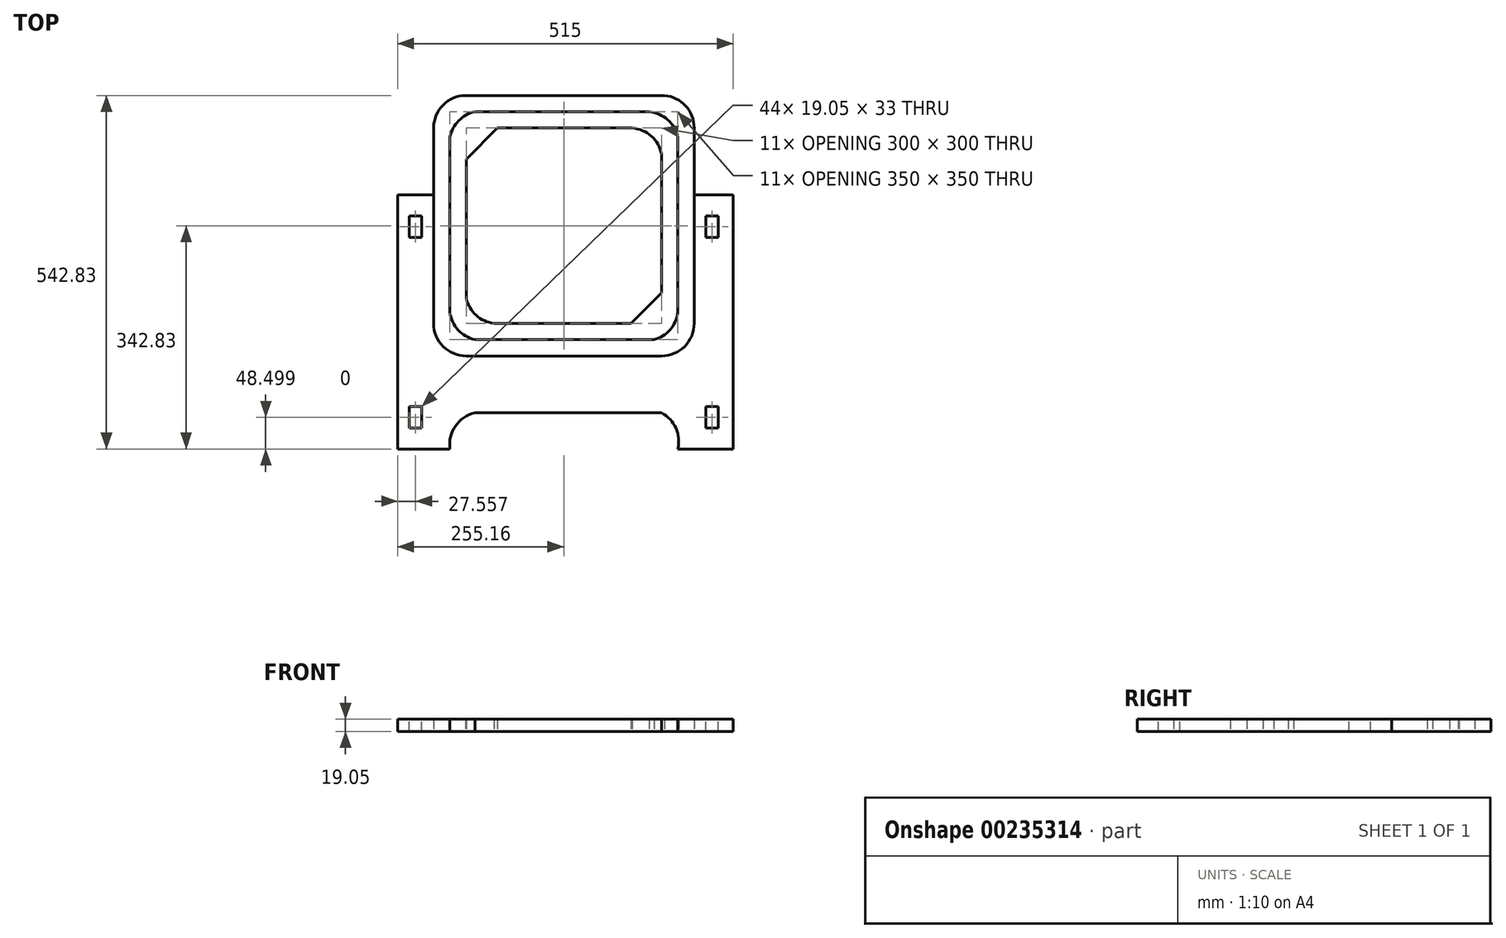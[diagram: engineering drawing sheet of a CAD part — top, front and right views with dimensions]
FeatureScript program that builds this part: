
annotation { "Feature Type Name" : "Feature", "Feature Type Description" : "" }
export const myFeature = defineFeature(function(context is Context, id is Id, definition is map)
    precondition{}
    {
        {
            var Q0;
            Q0=qCreatedBy(makeId("Top.planeOp"),FACE);
            var sketch = newSketch(context, id + "F0", { "sketchPlane" : qUnion([Q0])});
            skLineSegment(sketch, "E0.bottom", {"start": v(-150.99, 200) * mm, "end": v(154.38, 200) * mm});
            skLineSegment(sketch, "E0.top", {"start": v(-150, -200) * mm, "end": v(150, -200) * mm});
            skLineSegment(sketch, "E0.left", {"start": v(-200, 150.95) * mm, "end": v(-200, -150) * mm});
            skLineSegment(sketch, "E0.right", {"start": v(200, 150.38) * mm, "end": v(200, -150) * mm});
            skPoint(sketch, "E0.middle", {"position": v(0, 0) * mm});
            skLineSegment(sketch, "E1.bottom", {"start": v(-136.63, 175) * mm, "end": v(130.7, 175) * mm});
            skLineSegment(sketch, "E1.top", {"start": v(-136.63, -175) * mm, "end": v(138.66, -175) * mm});
            skLineSegment(sketch, "E1.left", {"start": v(-175, 136.37) * mm, "end": v(-175, -133.3) * mm});
            skLineSegment(sketch, "E1.right", {"start": v(175, 136.37) * mm, "end": v(175, -133.3) * mm});
            skLineSegment(sketch, "E2.bottom", {"start": v(-102.26, 150) * mm, "end": v(104.86, 150) * mm});
            skLineSegment(sketch, "E2.top", {"start": v(-107.07, -150) * mm, "end": v(102.92, -150) * mm});
            skLineSegment(sketch, "E2.left", {"start": v(-150, 102.12) * mm, "end": v(-150, -111.41) * mm});
            skLineSegment(sketch, "E2.right", {"start": v(150, 110.12) * mm, "end": v(150, -102.78) * mm});
            skLineSegment(sketch, "E3.bottom", {"start": v(-255.16, -342.83) * mm, "end": v(-175, -342.83) * mm});
            skLineSegment(sketch, "E3.top", {"start": v(-255.16, 47.17) * mm, "end": v(-200, 47.17) * mm});
            skLineSegment(sketch, "E3.left", {"start": v(-255.16, -342.83) * mm, "end": v(-255.16, 47.17) * mm});
            skLineSegment(sketch, "E3.right", {"start": v(259.84, -342.83) * mm, "end": v(259.84, 47.17) * mm});
            skArc(sketch, "E4", {"start": v(-149.03, 200) * mm, "mid": v(-184.68, 186.04) * mm, "end": v(-200, 150.95) * mm});
            skArc(sketch, "E5", {"start": v(200, 150) * mm, "mid": v(183.84, 187) * mm, "end": v(145.62, 200) * mm});
            skArc(sketch, "E6", {"start": v(-200, -150) * mm, "mid": v(-185.36, -185.36) * mm, "end": v(-150, -200) * mm});
            skArc(sketch, "E7", {"start": v(150, -200) * mm, "mid": v(185.36, -185.36) * mm, "end": v(200, -150) * mm});
            skPoint(sketch, "E8.orphan", {"position": v(200, -200) * mm});
            skPoint(sketch, "E9.orphan", {"position": v(-200, -200) * mm});
            skPoint(sketch, "E10.orphan", {"position": v(200, 200) * mm});
            skPoint(sketch, "E11.orphan", {"position": v(-200, 200) * mm});
            skArc(sketch, "E12", {"start": v(-136.63, 175) * mm, "mid": v(-161.54, 161.36) * mm, "end": v(-175, 136.37) * mm});
            skArc(sketch, "E13", {"start": v(175, 136.37) * mm, "mid": v(159.13, 162.88) * mm, "end": v(130.7, 175) * mm});
            skArc(sketch, "E14", {"start": v(-175, -133.3) * mm, "mid": v(-162.3, -160.1) * mm, "end": v(-136.63, -175) * mm});
            skArc(sketch, "E15", {"start": v(138.66, -175) * mm, "mid": v(163.12, -159.63) * mm, "end": v(175, -133.3) * mm});
            skArc(sketch, "E16", {"start": v(-136.63, -287.4) * mm, "mid": v(-166.56, -307.67) * mm, "end": v(-175, -342.83) * mm});
            skArc(sketch, "E17", {"start": v(175, -342.83) * mm, "mid": v(171.9, -310.87) * mm, "end": v(150, -287.4) * mm});
            skLineSegment(sketch, "E18", {"start": v(-136.63, -287.4) * mm, "end": v(150, -287.4) * mm});
            skLineSegment(sketch, "E19.trimOffspring", {"start": v(175, -342.83) * mm, "end": v(259.84, -342.83) * mm});
            skArc(sketch, "E20", {"start": v(150, 110.12) * mm, "mid": v(134.1, 137.62) * mm, "end": v(104.86, 150) * mm});
            skArc(sketch, "E21", {"start": v(-150, -111.41) * mm, "mid": v(-134.67, -137.53) * mm, "end": v(-107.07, -150) * mm});
            skCircle(sketch, "E22", {"center": v(-54.99, 56.8) * mm, "radius": 42.5 * mm});
            skCircle(sketch, "E23", {"center": v(-54.99, -35.11) * mm, "radius": 27.5 * mm});
            skArc(sketch, "E24", {"start": v(35.46, 73.38) * mm, "mid": v(20.46, 88.38) * mm, "end": v(5.46, 73.38) * mm});
            skArc(sketch, "E25", {"start": v(45.8, -43.7) * mm, "mid": v(60.8, -58.7) * mm, "end": v(75.8, -43.7) * mm});
            skArc(sketch, "E26", {"start": v(43.9, 89.17) * mm, "mid": v(37.47, 72.1) * mm, "end": v(45.8, 55.87) * mm});
            skArc(sketch, "E27", {"start": v(5.46, -26.92) * mm, "mid": v(-2.03, -42.98) * mm, "end": v(4.43, -59.48) * mm});
            skLineSegment(sketch, "E28", {"start": v(75.8, -43.7) * mm, "end": v(75.8, 57.42) * mm});
            skLineSegment(sketch, "E29", {"start": v(45.8, -43.7) * mm, "end": v(45.8, 55.87) * mm});
            skLineSegment(sketch, "E30", {"start": v(35.46, 73.38) * mm, "end": v(35.46, -26.92) * mm});
            skLineSegment(sketch, "E31", {"start": v(5.46, 73.38) * mm, "end": v(5.46, -26.92) * mm});
            skArc(sketch, "E32", {"start": v(72.87, -93.57) * mm, "mid": v(96.16, -81.07) * mm, "end": v(72.87, -68.57) * mm});
            skArc(sketch, "E33", {"start": v(-16.83, -68.57) * mm, "mid": v(-29.33, -81.07) * mm, "end": v(-16.83, -93.57) * mm});
            skLineSegment(sketch, "E34", {"start": v(-16.83, -68.57) * mm, "end": v(72.87, -68.57) * mm});
            skLineSegment(sketch, "E35", {"start": v(-16.83, -93.57) * mm, "end": v(72.87, -93.57) * mm});
            skArc(sketch, "E36.trimOffspring", {"start": v(75.8, 57.42) * mm, "mid": v(82.43, 73.26) * mm, "end": v(75.96, 89.17) * mm});
            skPoint(sketch, "E37.start.orphan", {"position": v(59.93, 89.17) * mm});
            skLineSegment(sketch, "E38", {"start": v(43.9, 89.17) * mm, "end": v(75.96, 89.17) * mm});
            skLineSegment(sketch, "E39", {"start": v(59.93, 73.38) * mm, "end": v(59.93, 89.17) * mm, "construction": true});
            skArc(sketch, "E40.trimOffspring", {"start": v(36.48, -59.48) * mm, "mid": v(42.94, -42.98) * mm, "end": v(35.46, -26.92) * mm});
            skLineSegment(sketch, "E41", {"start": v(4.43, -59.48) * mm, "end": v(36.48, -59.48) * mm});
            skLineSegment(sketch, "E42", {"start": v(125.43, -126.78) * mm, "end": v(150, -150) * mm, "construction": true});
            skLineSegment(sketch, "E43", {"start": v(-126.06, 126.13) * mm, "end": v(-150, 102.12) * mm});
            skLineSegment(sketch, "E44", {"start": v(-126.06, 126.13) * mm, "end": v(-102.26, 150) * mm});
            skLineSegment(sketch, "E45", {"start": v(126.63, -126.22) * mm, "end": v(102.7, -150.23) * mm});
            skLineSegment(sketch, "E46", {"start": v(126.63, -126.22) * mm, "end": v(150.43, -102.35) * mm});
            skLineSegment(sketch, "E47.trimOffspring", {"start": v(200, 47.17) * mm, "end": v(259.84, 47.17) * mm});
            skPoint(sketch, "E48.orphan", {"position": v(-175, 175) * mm});
            skPoint(sketch, "E49.orphan", {"position": v(175, 175) * mm});
            skPoint(sketch, "E50.orphan", {"position": v(175, -175) * mm});
            skPoint(sketch, "E51.orphan", {"position": v(-175, -175) * mm});
            skPoint(sketch, "E52.orphan", {"position": v(150, 150) * mm});
            skLineSegment(sketch, "E53.bottom", {"start": v(-110, 110) * mm, "end": v(110, 110) * mm});
            skLineSegment(sketch, "E53.top", {"start": v(-110, -110) * mm, "end": v(110, -110) * mm});
            skLineSegment(sketch, "E53.left", {"start": v(-110, 110) * mm, "end": v(-110, -110) * mm});
            skLineSegment(sketch, "E53.right", {"start": v(110, 110) * mm, "end": v(110, -110) * mm});
            skLineSegment(sketch, "E54", {"start": v(-110, -110) * mm, "end": v(-92.32, -92.32) * mm});
            skLineSegment(sketch, "E55", {"start": v(-74.64, -110) * mm, "end": v(-110, -74.64) * mm});
            skLineSegment(sketch, "E56", {"start": v(110, 73.38) * mm, "end": v(75.96, 110) * mm});
            skLineSegment(sketch, "E57.trimOffspring", {"start": v(92.36, 92.36) * mm, "end": v(110, 110) * mm});
            skSolve(sketch);
        }
        {
            var Q0;
            Q0=makeQuery(id+"F0.imprint","IMPRINT",FACE,{"disambiguationData":[TD([[makeQuery(id+"F0.imprint","IMPRINT",EDGE,{"derivedFrom":sQuery(id+"F0.wireOp",EDGE,"E0.top")}),-1.0]])]});
            extrude(context, id + "F1", {"entities" : qUnion([Q0]), "depth" : 19.05 * mm});
        }
        {
            var Q0;
            Q0=makeQuery(id+"F0.imprint","IMPRINT",FACE,{"disambiguationData":[TD([[makeQuery(id+"F0.imprint","IMPRINT",EDGE,{"derivedFrom":sQuery(id+"F0.wireOp",EDGE,"E0.top")}),1.0]])]});
            extrude(context, id + "F2", {"entities" : qUnion([Q0]), "depth" : 19.05 * mm});
        }
        {
            var Q0;
            Q0=makeQuery(id+"F0.imprint","IMPRINT",FACE,{"disambiguationData":[TD([[makeQuery(id+"F0.imprint","IMPRINT",EDGE,{"derivedFrom":sQuery(id+"F0.wireOp",EDGE,"E1.bottom")}),-1.0]])]});
            extrude(context, id + "F3", {"entities" : qUnion([Q0]), "depth" : 19.05 * mm});
        }
        {
            var Q0;
            Q0=makeQuery(id+"F1.opExtrude","CAP_FACE",FACE,{"disambiguationData":[OSD([sQuery(id+"F0.wireOp",EDGE,"E0.top"),sQuery(id+"F0.wireOp",EDGE,"E0.left"),sQuery(id+"F0.wireOp",EDGE,"E0.right"),sQuery(id+"F0.wireOp",EDGE,"E3.bottom"),sQuery(id+"F0.wireOp",EDGE,"E3.top"),sQuery(id+"F0.wireOp",EDGE,"E3.left"),sQuery(id+"F0.wireOp",EDGE,"E3.right"),sQuery(id+"F0.wireOp",EDGE,"E6"),sQuery(id+"F0.wireOp",EDGE,"E7"),sQuery(id+"F0.wireOp",EDGE,"E16"),sQuery(id+"F0.wireOp",EDGE,"E17"),sQuery(id+"F0.wireOp",EDGE,"E18"),sQuery(id+"F0.wireOp",EDGE,"E19.trimOffspring"),sQuery(id+"F0.wireOp",EDGE,"E47.trimOffspring")])],"isStart":false});
            var sketch = newSketch(context, id + "F4", { "sketchPlane" : qUnion([Q0])});
            skLineSegment(sketch, "E58.bottom", {"start": v(-237.13, 15.17) * mm, "end": v(-218.08, 15.17) * mm});
            skLineSegment(sketch, "E58.top", {"start": v(-237.13, -17.83) * mm, "end": v(-218.08, -17.83) * mm});
            skLineSegment(sketch, "E58.left", {"start": v(-237.13, 15.17) * mm, "end": v(-237.13, -17.83) * mm});
            skLineSegment(sketch, "E58.right", {"start": v(-218.08, 15.17) * mm, "end": v(-218.08, -17.83) * mm});
            skLineSegment(sketch, "E59", {"start": v(-227.58, 47.17) * mm, "end": v(-227.58, -342.83) * mm, "construction": true});
            skPoint(sketch, "E59.endSnap0", {"position": v(-215.08, -342.83) * mm});
            skLineSegment(sketch, "E60.bottom", {"start": v(-237.13, -277.83) * mm, "end": v(-218.08, -277.83) * mm});
            skLineSegment(sketch, "E60.top", {"start": v(-237.13, -310.83) * mm, "end": v(-218.08, -310.83) * mm});
            skLineSegment(sketch, "E60.left", {"start": v(-237.13, -277.83) * mm, "end": v(-237.13, -310.83) * mm});
            skLineSegment(sketch, "E60.right", {"start": v(-218.08, -277.83) * mm, "end": v(-218.08, -310.83) * mm});
            skLineSegment(sketch, "E61", {"start": v(0, -341.78) * mm, "end": v(0, 201.78) * mm, "construction": true});
            skLineSegment(sketch, "E62.MirrorCS", {"start": v(218.08, 15.17) * mm, "end": v(218.08, -17.83) * mm});
            skLineSegment(sketch, "E63.MirrorCS", {"start": v(237.13, -17.83) * mm, "end": v(218.08, -17.83) * mm});
            skLineSegment(sketch, "E64.MirrorCS", {"start": v(237.13, 15.17) * mm, "end": v(237.13, -17.83) * mm});
            skLineSegment(sketch, "E65.MirrorCS", {"start": v(237.13, 15.17) * mm, "end": v(218.08, 15.17) * mm});
            skLineSegment(sketch, "E66.MirrorCS", {"start": v(237.13, -277.83) * mm, "end": v(218.08, -277.83) * mm});
            skLineSegment(sketch, "E67.MirrorCS", {"start": v(218.08, -277.83) * mm, "end": v(218.08, -310.83) * mm});
            skLineSegment(sketch, "E68.MirrorCS", {"start": v(237.13, -310.83) * mm, "end": v(218.08, -310.83) * mm});
            skLineSegment(sketch, "E69.MirrorCS", {"start": v(237.13, -277.83) * mm, "end": v(237.13, -310.83) * mm});
            skSolve(sketch);
        }
        {
            var Q0;
            Q0 = qSketchRegion(id + "F4", true);
            extrude(context, id + "F5", {"entities" : qUnion([Q0]), "operationType" : NewBodyOperationType.REMOVE, "endBound" : BoundingType.THROUGH_ALL, "oppositeDirection" : true, "depth" : 25 * mm});
        }
    });
